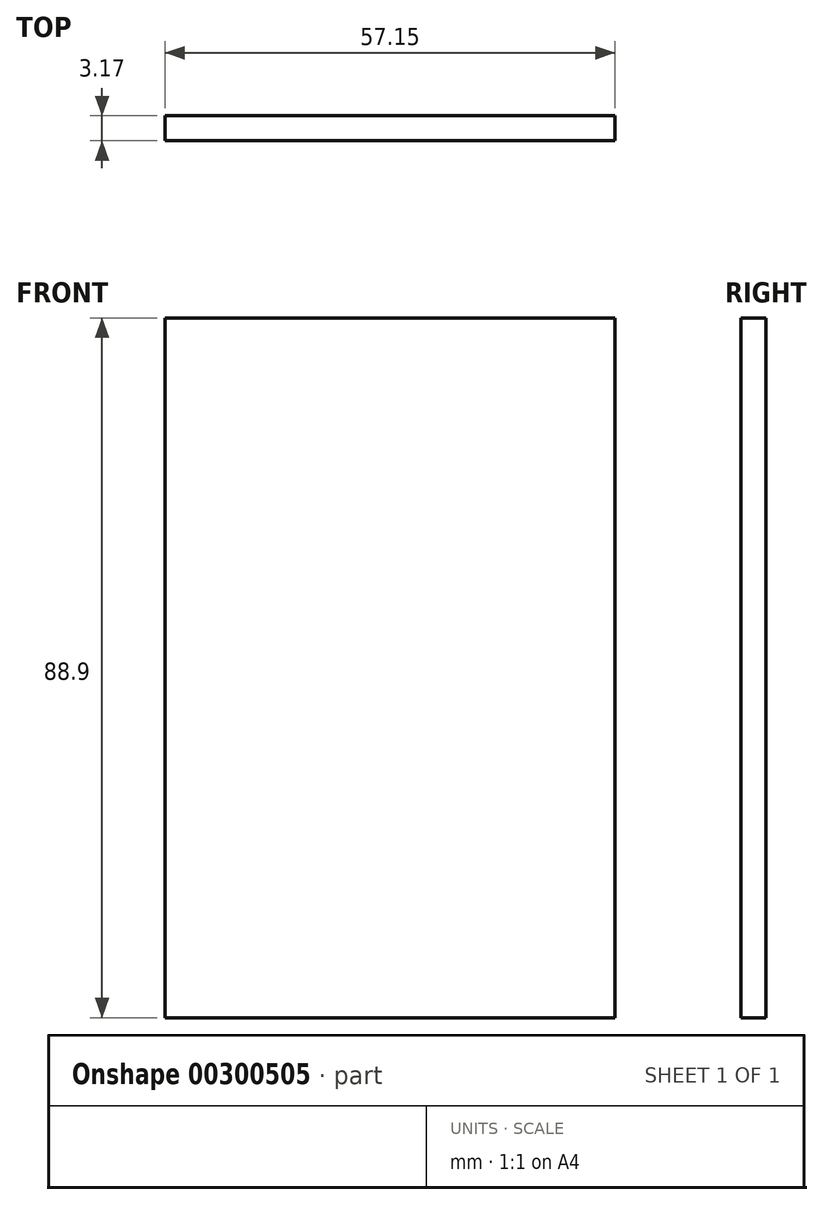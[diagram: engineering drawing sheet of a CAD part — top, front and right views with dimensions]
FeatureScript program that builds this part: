
annotation { "Feature Type Name" : "Feature", "Feature Type Description" : "" }
export const myFeature = defineFeature(function(context is Context, id is Id, definition is map)
    precondition{}
    {
        {
            var Q0;
            Q0=qCreatedBy(makeId("Front.planeOp"),FACE);
            var sketch = newSketch(context, id + "F0", { "sketchPlane" : qUnion([Q0])});
            skLineSegment(sketch, "E0.bottom", {"start": v(-27.95, 38.27) * mm, "end": v(29.2, 38.27) * mm});
            skLineSegment(sketch, "E0.top", {"start": v(-27.95, -50.63) * mm, "end": v(29.2, -50.63) * mm});
            skLineSegment(sketch, "E0.left", {"start": v(-27.95, 38.27) * mm, "end": v(-27.95, -50.63) * mm});
            skLineSegment(sketch, "E0.right", {"start": v(29.2, 38.27) * mm, "end": v(29.2, -50.63) * mm});
            skSolve(sketch);
        }
        {
            var Q0;
            Q0 = qSketchRegion(id + "F0", true);
            extrude(context, id + "F1", {"entities" : qUnion([Q0]), "depth" : 3.17 * mm});
        }
    });
